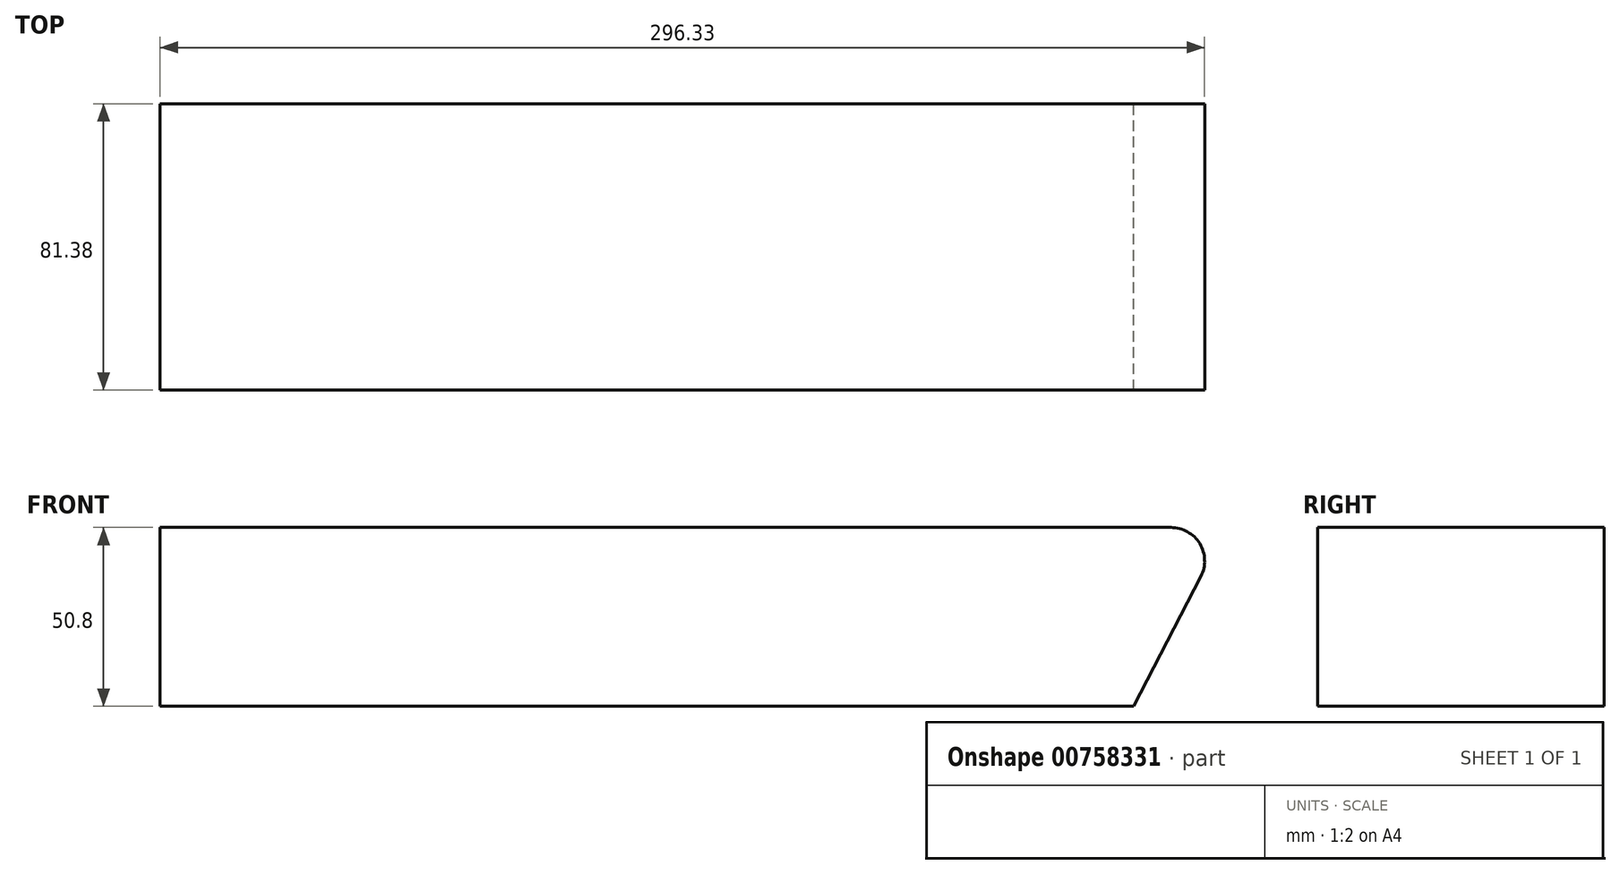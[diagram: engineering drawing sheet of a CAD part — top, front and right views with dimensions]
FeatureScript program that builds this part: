
annotation { "Feature Type Name" : "Feature", "Feature Type Description" : "" }
export const myFeature = defineFeature(function(context is Context, id is Id, definition is map)
    precondition{}
    {
        {
            var Q0;
            Q0=qCreatedBy(makeId("Front.planeOp"),FACE);
            var sketch = newSketch(context, id + "F0", { "sketchPlane" : qUnion([Q0])});
            skLineSegment(sketch, "E0", {"start": v(-202.72, 0) * mm, "end": v(-202.72, 50.8) * mm});
            skLineSegment(sketch, "E1", {"start": v(-202.72, 50.8) * mm, "end": v(84.09, 50.8) * mm});
            skLineSegment(sketch, "E2", {"start": v(92.55, 36.9) * mm, "end": v(73.5, 0) * mm});
            skLineSegment(sketch, "E3", {"start": v(73.5, 0) * mm, "end": v(-202.72, 0) * mm});
            skArc(sketch, "E4.filletArc", {"start": v(92.55, 36.9) * mm, "mid": v(92.22, 46.23) * mm, "end": v(84.09, 50.8) * mm});
            skSolve(sketch);
        }
        {
            var Q0;
            Q0=makeQuery(id+"F0.imprint","IMPRINT",FACE,{"disambiguationData":[TD([[makeQuery(id+"F0.imprint","IMPRINT",EDGE,{"derivedFrom":sQuery(id+"F0.wireOp",EDGE,"E0")}),-1.0]])]});
            extrude(context, id + "F1", {"entities" : qUnion([Q0]), "depth" : (81 + (3 / 8)) * mm, "offsetDistance" : 25.4 * mm});
        }
    });
